# Revit family: Legrand Export Universal Mini Columns
name_source: partatom
category: Installations électriques
units: mm (PartAtom-declared; Revit-internal decimal feet)

## family parameters
Basée sur le plan de construction = Non
Conserver l'orientation des annotations = Non
Cote de connecteur circulaire = Utiliser le diamètre
Couper avec des vides une fois chargée = Non
Partagée = Non
Point de calcul de pièce = Non
Toujours verticalement = Oui
Type d'élément = Normal

## types (12) — shared parameters
Fabricant = LEGRAND
Largeur = 75 mm
Main Material = Aluminum
Standard = Universal
Séparateur = 35 mm
zero-valued in all types: Elévation par défaut

## per-type parameters (varying)
| type | 1 CPT | 2 CPT | Black | Column stand | Description | Finishing | H1 | HC | Longueur | Matériau couvercle | Matériaux corps | Modèle | Number of compartments |
| Column 1 cpt CV80 0,3M White | Oui | Non | Non | Movable feet : Foot for mini Column White | universal mini Column 1 compartment 0,3m White | White | 300 mm | 260 mm  [stored 0.853018 ft] | 82 mm | Legrand - Plastique blanc | Legrand - Aluminium blanc | LG-653100 | 1 compartment |
| Column 1 cpt CV80 0,3M Alu | Oui | Non | Non | Movable feet : Foot for mini Column Alu | universal mini Column 1 compartment 0,3m Aluminium | Aluminum | 300 mm | 260 mm  [stored 0.853018 ft] | 82 mm | Legrand - Plastique gris | Legrand - Aluminium gris | LG-653101 | 1 compartment |
| Column 1 cpt CV80 0,68M White | Oui | Non | Non | Movable feet : Foot for mini Column White | universal mini Column 1 compartment 0,68m White | White | 680 mm  [stored 2.23097 ft] | 640 mm  [stored 2.09974 ft] | 82 mm | Legrand - Plastique blanc | Legrand - Aluminium blanc | LG-653103 | 1 compartment |
| Column 1 cpt CV80 0,68M Alu | Oui | Non | Non | Movable feet : Foot for mini Column Alu | universal mini Column 1 compartment 0,68m Aluminium | Aluminum | 680 mm  [stored 2.23097 ft] | 640 mm  [stored 2.09974 ft] | 82 mm | Legrand - Plastique gris | Legrand - Aluminium gris | LG-653104 | 1 compartment |
| Column 2 cpts 80 0,30M White | Non | Oui | Non | Movable feet : Foot for mini Column White | universal mini Column 2 compartments 0,30m White | White | 300 mm | 260 mm  [stored 0.853018 ft] | 125 mm | Legrand - Plastique blanc | Legrand - Aluminium blanc | LG-653120 | 2 compartments |
| Column 2 cpts CV80 0,30M Alu | Non | Oui | Non | Movable feet : Foot for mini Column Alu | universal mini Column 2 compartments 0,30m Aluminium | Aluminum | 300 mm | 260 mm  [stored 0.853018 ft] | 125 mm | Legrand - Plastique gris | Legrand - Aluminium gris | LG-653121 | 2 compartments |
| Column 2 cpts 80 0,68M White | Non | Oui | Non | Movable feet : Foot for mini Column White | universal mini Column 2 compartments 0,68m White | White | 680 mm  [stored 2.23097 ft] | 640 mm  [stored 2.09974 ft] | 125 mm | Legrand - Plastique blanc | Legrand - Aluminium blanc | LG-653123 | 2 compartments |
| Column 2 cpts CV80 0,68M Alu | Non | Oui | Non | Movable feet : Foot for mini Column Alu | universal mini Column 2 compartments 0,68m Aluminium | Aluminum | 680 mm  [stored 2.23097 ft] | 640 mm  [stored 2.09974 ft] | 125 mm | Legrand - Plastique gris | Legrand - Aluminium gris | LG-653124 | 2 compartments |
| Column 1 cpt CV80 0,68M Black | Oui | Non | Oui | Shelf : Table for mini Column T1/2 | universal mini Column 1 compartment 0,68m Black | Black | 680 mm  [stored 2.23097 ft] | 640 mm  [stored 2.09974 ft] | 82 mm | Legrand - Plastique noir | Legrand - Aluminium noir | LG-653105 | 1 compartment |
| Column 1 cpt CV80 0,3M Black | Oui | Non | Oui | Shelf : Table for mini Column T1/2 | universal mini Column 1 compartment 0,3m Black | Black | 300 mm | 260 mm  [stored 0.853018 ft] | 82 mm | Legrand - Plastique noir | Legrand - Aluminium noir | LG-653102 | 1 compartment |
| Column 2 cpts 80 0,30M Black | Oui | Oui | Non | Shelf : Table for mini Column T1/2 | universal mini Column 2 compartments 0,30m Black | Black | 300 mm | 260 mm  [stored 0.853018 ft] | 82 mm | Legrand - Plastique noir | Legrand - Aluminium noir | LG-653122 | 2 compartments |
| Column 2 cpts 80 0,68M Black | Non | Oui | Oui | Shelf : Table for mini Column T1/2 | universal mini Column 2 compartments 0,68m Black | Black | 680 mm  [stored 2.23097 ft] | 640 mm  [stored 2.09974 ft] | 125 mm | Legrand - Plastique noir | Legrand - Aluminium noir | LG-653125 | 2 compartments |

note: [stored X ft] marks values corroborated as IEEE doubles in the binary element streams (Revit-internal decimal feet)
